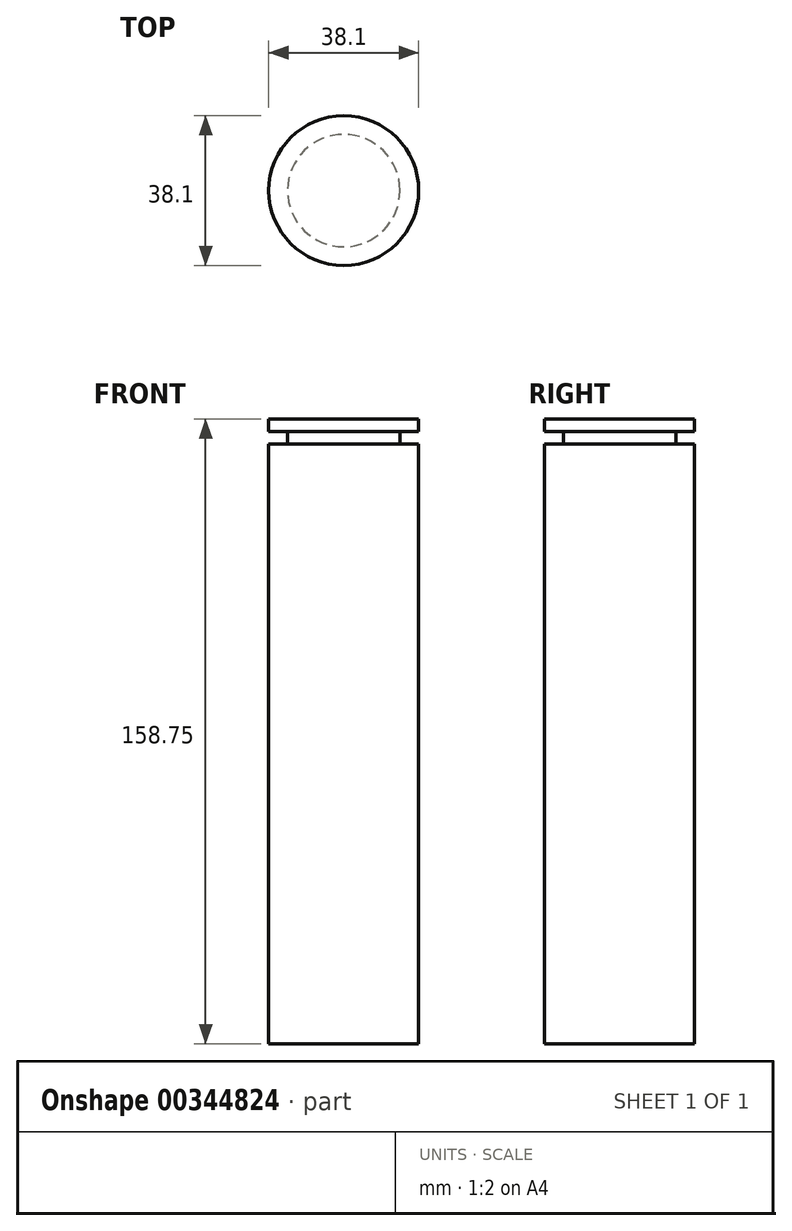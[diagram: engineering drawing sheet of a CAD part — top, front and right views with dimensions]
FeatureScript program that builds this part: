
annotation { "Feature Type Name" : "Feature", "Feature Type Description" : "" }
export const myFeature = defineFeature(function(context is Context, id is Id, definition is map)
    precondition{}
    {
        {
            var Q0;
            Q0=qCreatedBy(makeId("Top.planeOp"),FACE);
            var sketch = newSketch(context, id + "F0", { "sketchPlane" : qUnion([Q0])});
            skCircle(sketch, "E0", {"center": v(0, 0) * mm, "radius": 19.05 * mm});
            skSolve(sketch);
        }
        {
            var Q0;
            Q0=qSketchRegion(id+"F0",true);
            extrude(context, id + "F1", {"entities" : qUnion([Q0]), "oppositeDirection" : true, "depth" : 152.4 * mm});
        }
        {
            var Q0;
            Q0=makeQuery(id+"F1.opExtrude","CAP_FACE",FACE,{"disambiguationData":[OSD([sQuery(id+"F0.wireOp",EDGE,"E0")])],"isStart":true});
            var sketch = newSketch(context, id + "F2", { "sketchPlane" : qUnion([Q0])});
            skCircle(sketch, "E1", {"center": v(0, 0) * mm, "radius": 8 * mm, "construction": true});
            skCircle(sketch, "E2", {"center": v(0, 0) * mm, "radius": 14.29 * mm});
            skSolve(sketch);
        }
        {
            var Q0;
            Q0=makeQuery(id+"F2.imprint","IMPRINT",FACE,{"disambiguationData":[TD([[makeQuery(id+"F2.imprint","IMPRINT",EDGE,{"derivedFrom":sQuery(id+"F2.wireOp",EDGE,"E2")}),1.0]])]});
            extrude(context, id + "F3", {"entities" : qUnion([Q0]), "operationType" : NewBodyOperationType.ADD, "depth" : 3.17 * mm});
        }
        {
            var Q0;
            Q0=makeQuery(id+"F3.opExtrude","CAP_FACE",FACE,{"disambiguationData":[OSD([sQuery(id+"F2.wireOp",EDGE,"E2")])],"isStart":false});
            var sketch = newSketch(context, id + "F4", { "sketchPlane" : qUnion([Q0])});
            skCircle(sketch, "E3", {"center": v(0, 0) * mm, "radius": 19.05 * mm});
            skSolve(sketch);
        }
        {
            var Q0;
            Q0=qSketchRegion(id+"F4",true);
            extrude(context, id + "F5", {"entities" : qUnion([Q0]), "operationType" : NewBodyOperationType.ADD, "depth" : 3.17 * mm});
        }
    });
